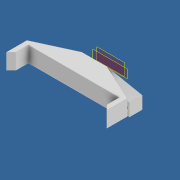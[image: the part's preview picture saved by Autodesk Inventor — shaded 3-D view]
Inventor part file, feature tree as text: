
AUTODESK INVENTOR PART (.ipt)
format: ipt  version: 2020 (Build 240168000, 168)  size: 199,680 bytes
history: native  units: mm
features: extrude x4, sketch x4, chamfer x3, plane x2, other x2, mirror x1, fillet x1, loft x1
ambient origin geometry x8: Origin, YZ Plane, XZ Plane, XY Plane, X Axis, Y Axis, Z Axis, Center Point
bodies: Solid1 (feature_tree)
feature tree (18):
  extrude  "Extrusion1"  Depth=10.0mm
  chamfer  "Chamfer1"  Distance=13.0mm
  chamfer  "Chamfer2"  Distance=24.0mm Angle=45.0deg
  extrude  "Extrusion2"  Depth=3.0mm
  chamfer  "Chamfer4"  Distance=11.0mm
  plane  "Work Plane1"
  mirror  "Mirror3"
  plane  "Work Plane8"
  extrude  "Extrusion9"  Depth=10.0mm
  extrude  "Extrusion10"  Depth=10.5mm
  fillet  "Fillet2"  Radius=24.0mm
  loft  "Loft7"
  sketch  "Sketch1"  dims[d1=64.0mm d2=10.0mm d3=13.0mm d4=0.0mm d5=24.0mm d6=11.0mm d7=45.0deg]
  sketch  "Sketch2"  dims[d8=24.0mm d9=11.0mm d10=45.0deg d14=3.0mm]
  sketch  "Sketch19"  dims[d15=10.0mm d16=11.0mm d17=0.0mm]
  sketch  "Sketch20"  dims[d18=3.0mm d19=10.0mm d20=45.0deg d21=10.0mm d94=10.5mm d95=24.0mm d96=8.0mm d97=13.0mm d98=8.0mm d99=0.0mm d100=5.0mm d101=5.0mm d102=5.0mm d103=8.0mm d104=8.0mm d105=4.0mm d106=8.0mm d107=0.0mm d108=0.7mm d109=0.0mm d110=90.0deg d111=0.0mm d112=90.0deg]
  other  "Edges5"
  other  "Edges6"
